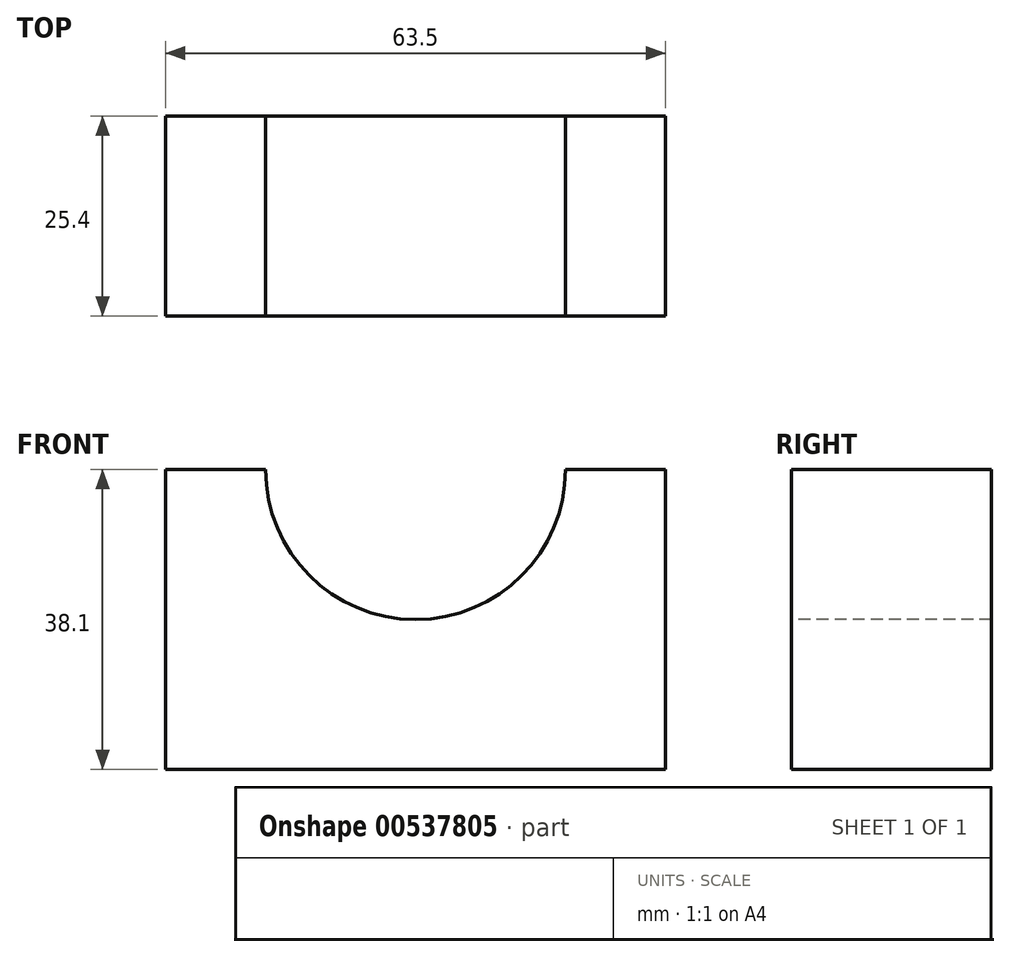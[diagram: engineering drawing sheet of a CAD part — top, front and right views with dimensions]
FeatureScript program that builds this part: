
annotation { "Feature Type Name" : "Feature", "Feature Type Description" : "" }
export const myFeature = defineFeature(function(context is Context, id is Id, definition is map)
    precondition{}
    {
        {
            var Q0;
            Q0=qCreatedBy(makeId("Front.planeOp"),FACE);
            var sketch = newSketch(context, id + "F0", { "sketchPlane" : qUnion([Q0])});
            skLineSegment(sketch, "E0", {"start": v(0, 0) * mm, "end": v(63.5, 0) * mm});
            skLineSegment(sketch, "E1", {"start": v(63.5, 0) * mm, "end": v(63.5, 38.1) * mm});
            skLineSegment(sketch, "E2", {"start": v(63.5, 38.1) * mm, "end": v(0, 38.1) * mm});
            skLineSegment(sketch, "E3", {"start": v(0, 38.1) * mm, "end": v(0, 0) * mm});
            skSolve(sketch);
        }
        {
            var Q0;
            Q0=makeQuery(id+"F0.imprint","IMPRINT",FACE,{"disambiguationData":[TD([[makeQuery(id+"F0.imprint","IMPRINT",EDGE,{"derivedFrom":sQuery(id+"F0.wireOp",EDGE,"E0")}),1.0]])]});
            extrude(context, id + "F1", {"entities" : qUnion([Q0]), "depth" : 25.4 * mm, "offsetDistance" : 25.4 * mm});
        }
        {
            var Q0;
            Q0=makeQuery(id+"F1.opExtrude","CAP_FACE",FACE,{"disambiguationData":[OSD([sQuery(id+"F0.wireOp",EDGE,"E0"),sQuery(id+"F0.wireOp",EDGE,"E1"),sQuery(id+"F0.wireOp",EDGE,"E2"),sQuery(id+"F0.wireOp",EDGE,"E3")])],"isStart":false});
            var sketch = newSketch(context, id + "F2", { "sketchPlane" : qUnion([Q0])});
            skLineSegment(sketch, "E4", {"start": v(0, 38.1) * mm, "end": v(12.7, 38.1) * mm});
            skLineSegment(sketch, "E5", {"start": v(63.5, 38.1) * mm, "end": v(49.21, 38.1) * mm});
            skCircle(sketch, "E6", {"center": v(31.75, 38.1) * mm, "radius": 19.05 * mm});
            skLineSegment(sketch, "E7", {"start": v(31.75, 0) * mm, "end": v(31.75, 19.05) * mm});
            skSolve(sketch);
        }
        {
            var Q0;
            {var subQ0=sQuery(id+"F2.wireOp",EDGE,"E5");var subQ1=makeQuery(id+"F1.opExtrude","CAP_EDGE",EDGE,{"disambiguationData":[OSD([sQuery(id+"F0.wireOp",EDGE,"E2")])],"isStart":false});var subQ2=makeQuery(id+"F2.imprint","INTERSECT",VERTEX,{"derivedFrom":[subQ1,subQ0]});Q0=makeQuery(id+"F2.imprint","IMPRINT",FACE,{"disambiguationData":[TD([[makeQuery(id+"F2.imprint","IMPRINT",EDGE,{"disambiguationData":[TD([[subQ2,1.0]])],"derivedFrom":subQ0}),1.0]])]});}
            extrude(context, id + "F3", {"entities" : qUnion([Q0]), "operationType" : NewBodyOperationType.REMOVE, "oppositeDirection" : true, "depth" : 25.4 * mm, "offsetDistance" : 25.4 * mm});
        }
    });
